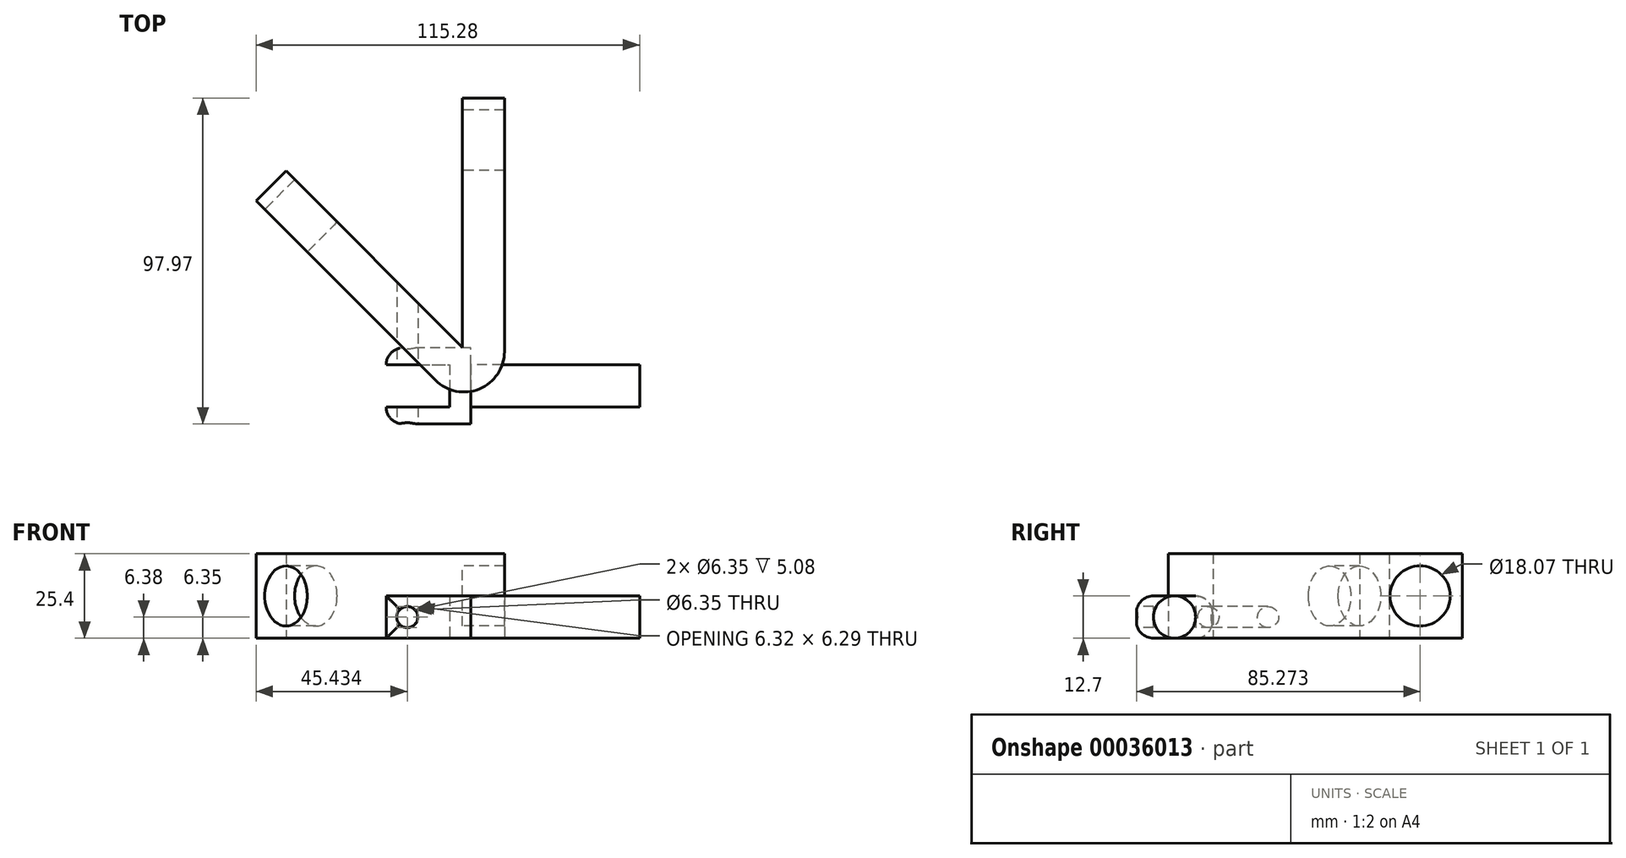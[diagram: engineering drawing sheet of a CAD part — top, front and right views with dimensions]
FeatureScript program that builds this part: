
annotation { "Feature Type Name" : "Feature", "Feature Type Description" : "" }
export const myFeature = defineFeature(function(context is Context, id is Id, definition is map)
    precondition{}
    {
        {
            var Q0;
            Q0=qCreatedBy(makeId("Top.planeOp"),FACE);
            var sketch = newSketch(context, id + "F0", { "sketchPlane" : qUnion([Q0])});
            skLineSegment(sketch, "E0", {"start": v(0, 74.91) * mm, "end": v(12.7, 74.91) * mm});
            skLineSegment(sketch, "E1", {"start": v(12.7, 74.91) * mm, "end": v(12.7, -1.29) * mm});
            skLineSegment(sketch, "E2", {"start": v(-8.07, -9.9) * mm, "end": v(-61.95, 44) * mm});
            skLineSegment(sketch, "E3", {"start": v(0, 74.91) * mm, "end": v(0, 0) * mm});
            skLineSegment(sketch, "E4", {"start": v(0, 0) * mm, "end": v(-52.97, 52.97) * mm});
            skLineSegment(sketch, "E5", {"start": v(-61.95, 44) * mm, "end": v(-52.97, 52.97) * mm});
            skPoint(sketch, "E6.visualSharp", {"position": v(12.7, -30.66) * mm});
            skArc(sketch, "E6.filletArc", {"start": v(-8.07, -9.9) * mm, "mid": v(5.19, -12.53) * mm, "end": v(12.7, -1.29) * mm});
            skSolve(sketch);
        }
        {
            var Q0;
            Q0 = qSketchRegion(id + "F0", true);
            extrude(context, id + "F1", {"entities" : qUnion([Q0]), "depth" : 25.4 * mm});
        }
        {
            var Q0;
            Q0=qCreatedBy(makeId("Right.planeOp"),FACE);
            var sketch = newSketch(context, id + "F2", { "sketchPlane" : qUnion([Q0])});
            skCircle(sketch, "E7", {"center": v(62.21, 12.7) * mm, "radius": 9.04 * mm});
            skSolve(sketch);
        }
        {
            var Q0;
            Q0 = qSketchRegion(id + "F2", true);
            var Q1;
            Q1=makeQuery(id+"F1.opExtrude","SWEPT_FACE",FACE,{"disambiguationData":[OSD([sQuery(id+"F0.wireOp",EDGE,"E1")])]});
            extrude(context, id + "F3", {"entities" : qUnion([Q0]), "operationType" : NewBodyOperationType.REMOVE, "endBound" : BoundingType.UP_TO_SURFACE, "endBoundEntityFace" : qUnion([Q1]), "depth" : 25.4 * mm});
        }
        {
            var Q0;
            Q0=makeQuery(id+"F1.opExtrude","SWEPT_FACE",FACE,{"disambiguationData":[OSD([sQuery(id+"F0.wireOp",EDGE,"E2")])]});
            var sketch = newSketch(context, id + "F4", { "sketchPlane" : qUnion([Q0])});
            skCircle(sketch, "E8", {"center": v(-62.21, 12.7) * mm, "radius": 9.03 * mm});
            skSolve(sketch);
        }
        {
            var Q0;
            Q0=makeQuery(id+"F4.imprint","IMPRINT",FACE,{"disambiguationData":[TD([[makeQuery(id+"F4.imprint","IMPRINT",EDGE,{"derivedFrom":sQuery(id+"F4.wireOp",EDGE,"E8")}),1.0]])]});
            var Q1;
            Q1=sQuery(id+"F4.wireOp",EDGE,"E8");
            var Q2;
            Q2=makeQuery(id+"F1.opExtrude","SWEPT_FACE",FACE,{"disambiguationData":[OSD([sQuery(id+"F0.wireOp",EDGE,"E4")])]});
            extrude(context, id + "F5", {"entities" : qUnion([Q0]), "operationType" : NewBodyOperationType.REMOVE, "surfaceEntities" : qUnion([Q1]), "endBound" : BoundingType.UP_TO_SURFACE, "oppositeDirection" : true, "endBoundEntityFace" : qUnion([Q2]), "depth" : 25.4 * mm});
        }
        {
            var Q0;
            Q0=qCreatedBy(makeId("Top.planeOp"),FACE);
            var sketch = newSketch(context, id + "F6", { "sketchPlane" : qUnion([Q0])});
            skLineSegment(sketch, "E9", {"start": v(-22.87, -17.98) * mm, "end": v(-22.87, -23.06) * mm});
            skLineSegment(sketch, "E10", {"start": v(-22.87, -23.06) * mm, "end": v(2.53, -23.06) * mm});
            skLineSegment(sketch, "E11", {"start": v(2.53, -23.06) * mm, "end": v(2.53, -0.2) * mm});
            skLineSegment(sketch, "E12", {"start": v(2.53, -0.2) * mm, "end": v(-22.87, -0.2) * mm});
            skLineSegment(sketch, "E13", {"start": v(-22.87, -0.2) * mm, "end": v(-22.87, -5.28) * mm});
            skLineSegment(sketch, "E14", {"start": v(-22.87, -5.28) * mm, "end": v(-3.82, -5.28) * mm});
            skLineSegment(sketch, "E15", {"start": v(-22.87, -17.98) * mm, "end": v(-3.82, -17.98) * mm});
            skLineSegment(sketch, "E16", {"start": v(-3.82, -5.28) * mm, "end": v(-3.82, -17.98) * mm});
            skSolve(sketch);
        }
        {
            var Q0;
            Q0=makeQuery(id+"F6.imprint","IMPRINT",FACE,{"disambiguationData":[TD([[makeQuery(id+"F6.imprint","IMPRINT",EDGE,{"derivedFrom":sQuery(id+"F6.wireOp",EDGE,"E9")}),1.0]])]});
            extrude(context, id + "F7", {"entities" : qUnion([Q0]), "depth" : 12.7 * mm});
        }
        {
            var Q0;
            Q0=makeQuery(id+"F7.opExtrude","SWEPT_FACE",FACE,{"disambiguationData":[OSD([sQuery(id+"F6.wireOp",EDGE,"E10")])]});
            var sketch = newSketch(context, id + "F8", { "sketchPlane" : qUnion([Q0])});
            skCircle(sketch, "E17", {"center": v(-16.52, 6.35) * mm, "radius": 3.17 * mm});
            skSolve(sketch);
        }
        {
            var Q0;
            Q0 = qSketchRegion(id + "F8", true);
            extrude(context, id + "F9", {"entities" : qUnion([Q0]), "operationType" : NewBodyOperationType.REMOVE, "endBound" : BoundingType.THROUGH_ALL, "oppositeDirection" : true, "depth" : 25.4 * mm});
        }
        {
            var Q0;
            Q0=makeQuery(id+"F7.opExtrude","SWEPT_FACE",FACE,{"disambiguationData":[OSD([sQuery(id+"F6.wireOp",EDGE,"E11")])]});
            var sketch = newSketch(context, id + "F10", { "sketchPlane" : qUnion([Q0])});
            skCircle(sketch, "E18", {"center": v(-11.63, 6.35) * mm, "radius": 6.35 * mm});
            skSolve(sketch);
        }
        {
            var Q0;
            Q0 = qSketchRegion(id + "F10", true);
            var Q1;
            Q1=sQuery(id+"F10.wireOp",EDGE,"E18");
            extrude(context, id + "F11", {"entities" : qUnion([Q0]), "surfaceEntities" : qUnion([Q1]), "depth" : 50.8 * mm});
        }
        {
            var Q0;
            Q0=makeQuery(id+"F7.opExtrude","CAP_EDGE",EDGE,{"disambiguationData":[OSD([sQuery(id+"F6.wireOp",EDGE,"E10")])],"isStart":false});
            var Q1;
            Q1=makeQuery(id+"F7.opExtrude","CAP_EDGE",EDGE,{"disambiguationData":[OSD([sQuery(id+"F6.wireOp",EDGE,"E10")])],"isStart":true});
            var Q2;
            Q2=makeQuery(id+"F7.opExtrude","SWEPT_EDGE",EDGE,{"disambiguationData":[OSD([sQuery(id+"F6.wireOp",EDGE,"E9"),sQuery(id+"F6.wireOp",EDGE,"E10")])]});
            var Q3;
            Q3=makeQuery(id+"F7.opExtrude","SWEPT_EDGE",EDGE,{"disambiguationData":[OSD([sQuery(id+"F6.wireOp",EDGE,"E12"),sQuery(id+"F6.wireOp",EDGE,"E13")])]});
            var Q4;
            Q4=makeQuery(id+"F7.opExtrude","CAP_EDGE",EDGE,{"disambiguationData":[OSD([sQuery(id+"F6.wireOp",EDGE,"E12")])],"isStart":true});
            var Q5;
            Q5=makeQuery(id+"F7.opExtrude","CAP_EDGE",EDGE,{"disambiguationData":[OSD([sQuery(id+"F6.wireOp",EDGE,"E12")])],"isStart":false});
            fillet(context, id + "F12", {"entities" : qUnion([Q0, Q1, Q2, Q3, Q4, Q5]), "radius" : 5.08 * mm, "tangentPropagation" : true, "allowEdgeOverflow" : false});
        }
    });
